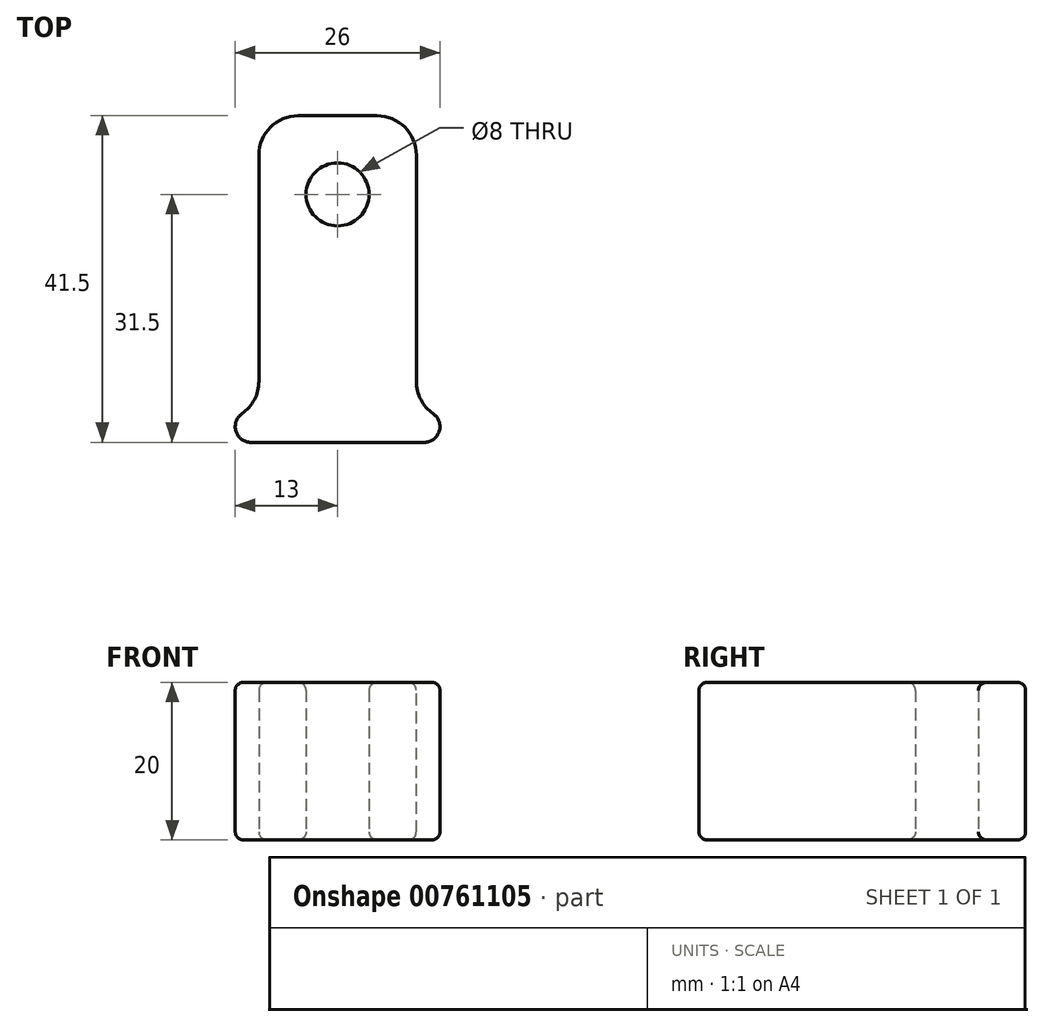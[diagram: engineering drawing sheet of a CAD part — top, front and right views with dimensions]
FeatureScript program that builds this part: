
annotation { "Feature Type Name" : "Feature", "Feature Type Description" : "" }
export const myFeature = defineFeature(function(context is Context, id is Id, definition is map)
    precondition{}
    {
        {
            var Q0;
            Q0=qCreatedBy(makeId("Top.planeOp"),FACE);
            var sketch = newSketch(context, id + "F0", { "sketchPlane" : qUnion([Q0])});
            skLineSegment(sketch, "E0.bottom", {"start": v(10, -20.75) * mm, "end": v(-10, -20.75) * mm});
            skLineSegment(sketch, "E0.top", {"start": v(10, 20.75) * mm, "end": v(-10, 20.75) * mm});
            skLineSegment(sketch, "E0.left", {"start": v(10, -16.75) * mm, "end": v(10, 20.75) * mm});
            skLineSegment(sketch, "E0.right", {"start": v(-10, -16.75) * mm, "end": v(-10, 20.75) * mm});
            skPoint(sketch, "E0.middle", {"position": v(0, 0) * mm});
            skCircle(sketch, "E1", {"center": v(0, 10.75) * mm, "radius": 4 * mm});
            skLineSegment(sketch, "E2.bottom", {"start": v(-10, -20.75) * mm, "end": v(-13, -20.75) * mm});
            skLineSegment(sketch, "E2.top", {"start": v(-10, -16.75) * mm, "end": v(-13, -16.75) * mm});
            skLineSegment(sketch, "E2.right", {"start": v(-13, -20.75) * mm, "end": v(-13, -16.75) * mm});
            skLineSegment(sketch, "E3.bottom", {"start": v(10, -20.75) * mm, "end": v(13, -20.75) * mm});
            skLineSegment(sketch, "E3.top", {"start": v(10, -16.75) * mm, "end": v(13, -16.75) * mm});
            skLineSegment(sketch, "E3.right", {"start": v(13, -20.75) * mm, "end": v(13, -16.75) * mm});
            skSolve(sketch);
        }
        {
            var Q0;
            Q0=makeQuery(id+"F0.imprint","IMPRINT",FACE,{"disambiguationData":[TD([[makeQuery(id+"F0.imprint","IMPRINT",EDGE,{"derivedFrom":sQuery(id+"F0.wireOp",EDGE,"E0.bottom")}),-1.0]])]});
            extrude(context, id + "F1", {"entities" : qUnion([Q0]), "depth" : 20 * mm, "offsetDistance" : 25 * mm});
        }
        {
            var Q0;
            Q0=makeQuery(id+"F1.opExtrude","SWEPT_EDGE",EDGE,{"disambiguationData":[OSD([sQuery(id+"F0.wireOp",EDGE,"E0.top"),sQuery(id+"F0.wireOp",EDGE,"E0.right")])]});
            var Q1;
            Q1=makeQuery(id+"F1.opExtrude","SWEPT_EDGE",EDGE,{"disambiguationData":[OSD([sQuery(id+"F0.wireOp",EDGE,"E0.top"),sQuery(id+"F0.wireOp",EDGE,"E0.left")])]});
            fillet(context, id + "F2", {"entities" : qUnion([Q0, Q1]), "radius" : 5 * mm, "tangentPropagation" : true, "allowEdgeOverflow" : false});
        }
        {
            var Q0;
            Q0=makeQuery(id+"F1.opExtrude","SWEPT_EDGE",EDGE,{"disambiguationData":[OSD([sQuery(id+"F0.wireOp",EDGE,"E2.top"),sQuery(id+"F0.wireOp",EDGE,"E2.right")])]});
            var Q1;
            Q1=makeQuery(id+"F1.opExtrude","SWEPT_EDGE",EDGE,{"disambiguationData":[OSD([sQuery(id+"F0.wireOp",EDGE,"E2.bottom"),sQuery(id+"F0.wireOp",EDGE,"E2.right")])]});
            var Q2;
            Q2=makeQuery(id+"F1.opExtrude","SWEPT_EDGE",EDGE,{"disambiguationData":[OSD([sQuery(id+"F0.wireOp",EDGE,"E3.top"),sQuery(id+"F0.wireOp",EDGE,"E3.right")])]});
            var Q3;
            Q3=makeQuery(id+"F1.opExtrude","SWEPT_EDGE",EDGE,{"disambiguationData":[OSD([sQuery(id+"F0.wireOp",EDGE,"E3.bottom"),sQuery(id+"F0.wireOp",EDGE,"E3.right")])]});
            fillet(context, id + "F3", {"entities" : qUnion([Q0, Q1, Q2, Q3]), "radius" : 2 * mm, "tangentPropagation" : true, "allowEdgeOverflow" : false});
        }
        {
            var Q0;
            Q0=makeQuery(id+"F1.opExtrude","SWEPT_EDGE",EDGE,{"disambiguationData":[OSD([sQuery(id+"F0.wireOp",EDGE,"E0.right"),sQuery(id+"F0.wireOp",EDGE,"E2.top")])]});
            var Q1;
            Q1=makeQuery(id+"F1.opExtrude","SWEPT_EDGE",EDGE,{"disambiguationData":[OSD([sQuery(id+"F0.wireOp",EDGE,"E0.left"),sQuery(id+"F0.wireOp",EDGE,"E3.top")])]});
            fillet(context, id + "F4", {"entities" : qUnion([Q0, Q1]), "radius" : 5 * mm, "tangentPropagation" : true, "allowEdgeOverflow" : false});
        }
        {
            var Q0;
            Q0=makeQuery(id+"F1.opExtrude","CAP_FACE",FACE,{"disambiguationData":[OSD([sQuery(id+"F0.wireOp",EDGE,"E0.bottom"),sQuery(id+"F0.wireOp",EDGE,"E0.top"),sQuery(id+"F0.wireOp",EDGE,"E0.left"),sQuery(id+"F0.wireOp",EDGE,"E0.right"),sQuery(id+"F0.wireOp",EDGE,"E1"),sQuery(id+"F0.wireOp",EDGE,"E2.bottom"),sQuery(id+"F0.wireOp",EDGE,"E2.top"),sQuery(id+"F0.wireOp",EDGE,"E2.right"),sQuery(id+"F0.wireOp",EDGE,"E3.bottom"),sQuery(id+"F0.wireOp",EDGE,"E3.top"),sQuery(id+"F0.wireOp",EDGE,"E3.right")])],"isStart":false});
            var Q1;
            Q1=makeQuery(id+"F1.opExtrude","CAP_FACE",FACE,{"disambiguationData":[OSD([sQuery(id+"F0.wireOp",EDGE,"E0.bottom"),sQuery(id+"F0.wireOp",EDGE,"E0.top"),sQuery(id+"F0.wireOp",EDGE,"E0.left"),sQuery(id+"F0.wireOp",EDGE,"E0.right"),sQuery(id+"F0.wireOp",EDGE,"E1"),sQuery(id+"F0.wireOp",EDGE,"E2.bottom"),sQuery(id+"F0.wireOp",EDGE,"E2.top"),sQuery(id+"F0.wireOp",EDGE,"E2.right"),sQuery(id+"F0.wireOp",EDGE,"E3.bottom"),sQuery(id+"F0.wireOp",EDGE,"E3.top"),sQuery(id+"F0.wireOp",EDGE,"E3.right")])],"isStart":true});
            fillet(context, id + "F5", {"entities" : qUnion([Q0, Q1]), "radius" : 1 * mm, "tangentPropagation" : true, "allowEdgeOverflow" : false});
        }
    });
